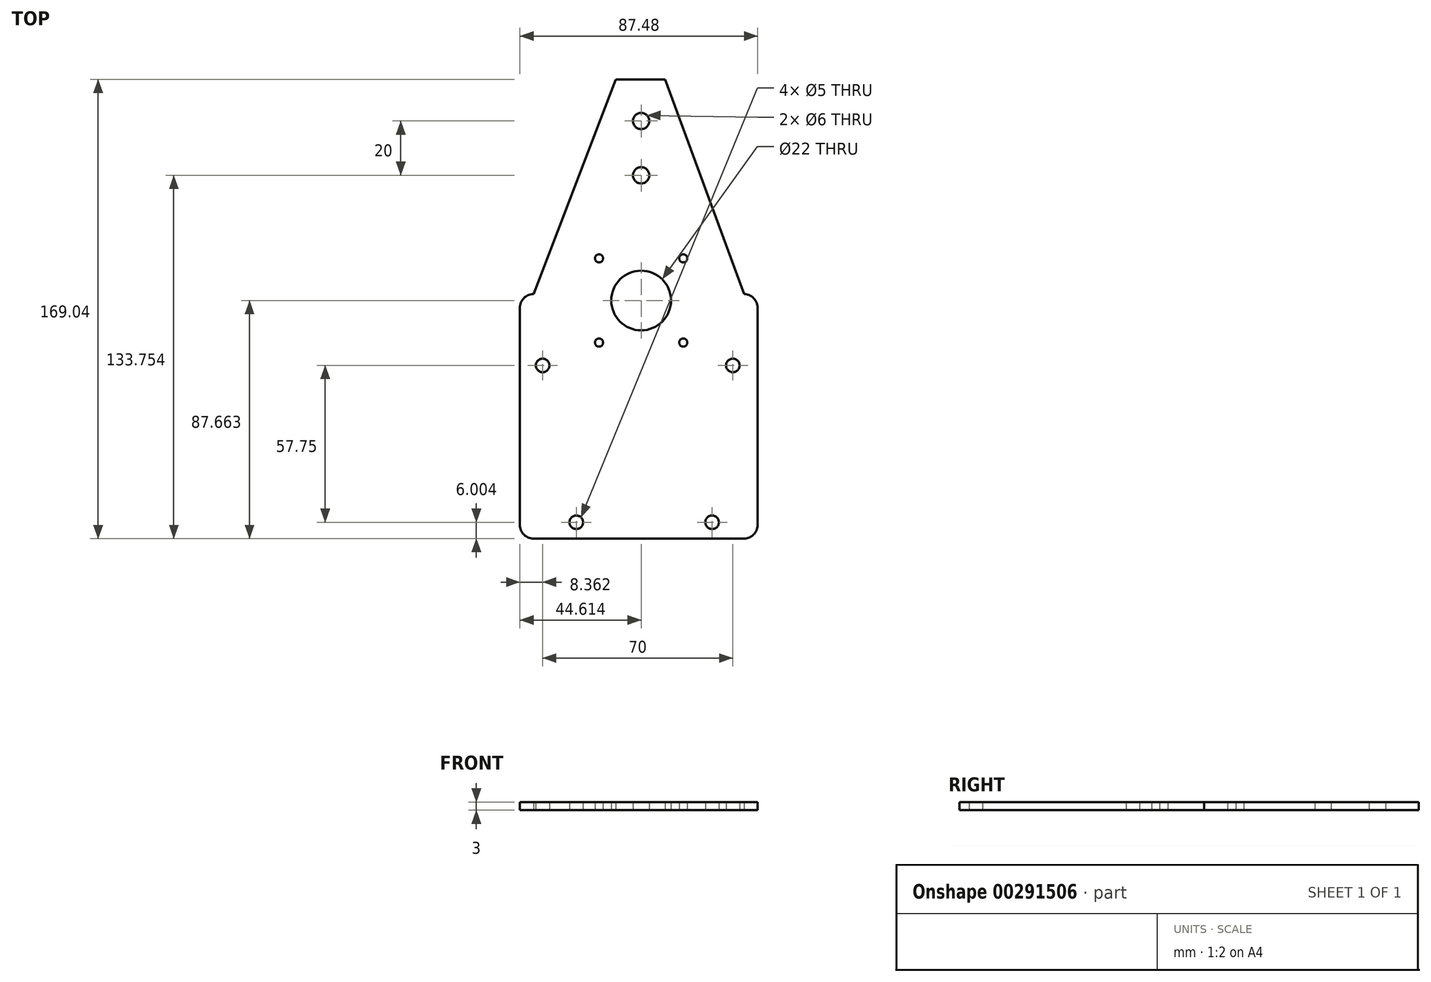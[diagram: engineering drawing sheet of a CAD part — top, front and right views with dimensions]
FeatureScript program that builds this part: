
annotation { "Feature Type Name" : "Feature", "Feature Type Description" : "" }
export const myFeature = defineFeature(function(context is Context, id is Id, definition is map)
    precondition{}
    {
        {
            var Q0;
            Q0=qCreatedBy(makeId("Top.planeOp"),FACE);
            var sketch = newSketch(context, id + "F0", { "sketchPlane" : qUnion([Q0])});
            skCircle(sketch, "E0", {"center": v(-45.06, -6.33) * mm, "radius": 10.5 * mm, "construction": true});
            skCircle(sketch, "E1", {"center": v(24.94, -6.33) * mm, "radius": 10.5 * mm, "construction": true});
            skLineSegment(sketch, "E2", {"start": v(-69.41, -6.33) * mm, "end": v(56.22, -6.33) * mm, "construction": true});
            skLineSegment(sketch, "E3", {"start": v(-66.98, -64.08) * mm, "end": v(56.02, -64.08) * mm, "construction": true});
            skCircle(sketch, "E4", {"center": v(-32.68, -64.08) * mm, "radius": 10.5 * mm, "construction": true});
            skCircle(sketch, "E5", {"center": v(17.32, -64.08) * mm, "radius": 10.5 * mm, "construction": true});
            skLineSegment(sketch, "E6.bottom", {"start": v(29.06, -70.08) * mm, "end": v(-48.42, -70.08) * mm});
            skLineSegment(sketch, "E6.left", {"start": v(34.06, -65.08) * mm, "end": v(34.06, 14.92) * mm});
            skLineSegment(sketch, "E6.right", {"start": v(-53.42, -65.08) * mm, "end": v(-53.42, 14.92) * mm});
            skPoint(sketch, "E7.visualSharp", {"position": v(-53.42, 6.93) * mm});
            skArc(sketch, "E7.filletArc", {"start": v(-48.42, 19.92) * mm, "mid": v(-51.96, 18.46) * mm, "end": v(-53.42, 14.92) * mm});
            skArc(sketch, "E8.filletArc", {"start": v(34.06, 14.92) * mm, "mid": v(32.6, 18.46) * mm, "end": v(29.06, 19.92) * mm});
            skArc(sketch, "E9.filletArc", {"start": v(29.06, -70.08) * mm, "mid": v(32.6, -68.61) * mm, "end": v(34.06, -65.08) * mm});
            skArc(sketch, "E10.filletArc", {"start": v(-53.42, -65.08) * mm, "mid": v(-51.96, -68.61) * mm, "end": v(-48.42, -70.08) * mm});
            skLineSegment(sketch, "E11", {"start": v(-48.42, 19.92) * mm, "end": v(-18.17, 98.96) * mm});
            skLineSegment(sketch, "E12", {"start": v(-18.17, 98.96) * mm, "end": v(0, 98.96) * mm});
            skLineSegment(sketch, "E13", {"start": v(0, 98.96) * mm, "end": v(29.06, 19.92) * mm});
            skCircle(sketch, "E14", {"center": v(-8.8, 83.67) * mm, "radius": 3 * mm});
            skCircle(sketch, "E15", {"center": v(-8.8, 63.67) * mm, "radius": 3 * mm});
            skCircle(sketch, "E16", {"center": v(-45.06, -6.33) * mm, "radius": 2.5 * mm});
            skCircle(sketch, "E17", {"center": v(24.94, -6.33) * mm, "radius": 2.5 * mm});
            skCircle(sketch, "E18", {"center": v(-32.68, -64.08) * mm, "radius": 2.5 * mm});
            skCircle(sketch, "E19", {"center": v(17.32, -64.08) * mm, "radius": 2.5 * mm});
            skCircle(sketch, "E20", {"center": v(-8.8, 17.58) * mm, "radius": 11 * mm});
            skLineSegment(sketch, "E21.bottom", {"start": v(-24.3, 33.08) * mm, "end": v(6.7, 33.08) * mm, "construction": true});
            skLineSegment(sketch, "E21.top", {"start": v(-24.3, 2.08) * mm, "end": v(6.7, 2.08) * mm, "construction": true});
            skLineSegment(sketch, "E21.left", {"start": v(-24.3, 33.08) * mm, "end": v(-24.3, 2.08) * mm, "construction": true});
            skLineSegment(sketch, "E21.right", {"start": v(6.7, 33.08) * mm, "end": v(6.7, 2.08) * mm, "construction": true});
            skLineSegment(sketch, "E22", {"start": v(-24.3, 33.08) * mm, "end": v(6.7, 2.08) * mm, "construction": true});
            skLineSegment(sketch, "E23", {"start": v(6.7, 33.08) * mm, "end": v(-24.3, 2.08) * mm, "construction": true});
            skCircle(sketch, "E24", {"center": v(-24.3, 33.08) * mm, "radius": 1.5 * mm});
            skLineSegment(sketch, "E25", {"start": v(-24.3, 17.58) * mm, "end": v(6.7, 17.58) * mm, "construction": true});
            skLineSegment(sketch, "E26", {"start": v(-8.8, 33.08) * mm, "end": v(-8.8, 2.08) * mm, "construction": true});
            skCircle(sketch, "E27.MirrorC", {"center": v(-24.3, 2.08) * mm, "radius": 1.5 * mm});
            skCircle(sketch, "E28.MirrorC", {"center": v(6.7, 2.08) * mm, "radius": 1.5 * mm});
            skCircle(sketch, "E29.MirrorC", {"center": v(6.7, 33.08) * mm, "radius": 1.5 * mm});
            skSolve(sketch);
        }
        {
            var Q0;
            Q0 = qSketchRegion(id + "F0", true);
            extrude(context, id + "F1", {"entities" : qUnion([Q0]), "depth" : 3 * mm});
        }
    });
